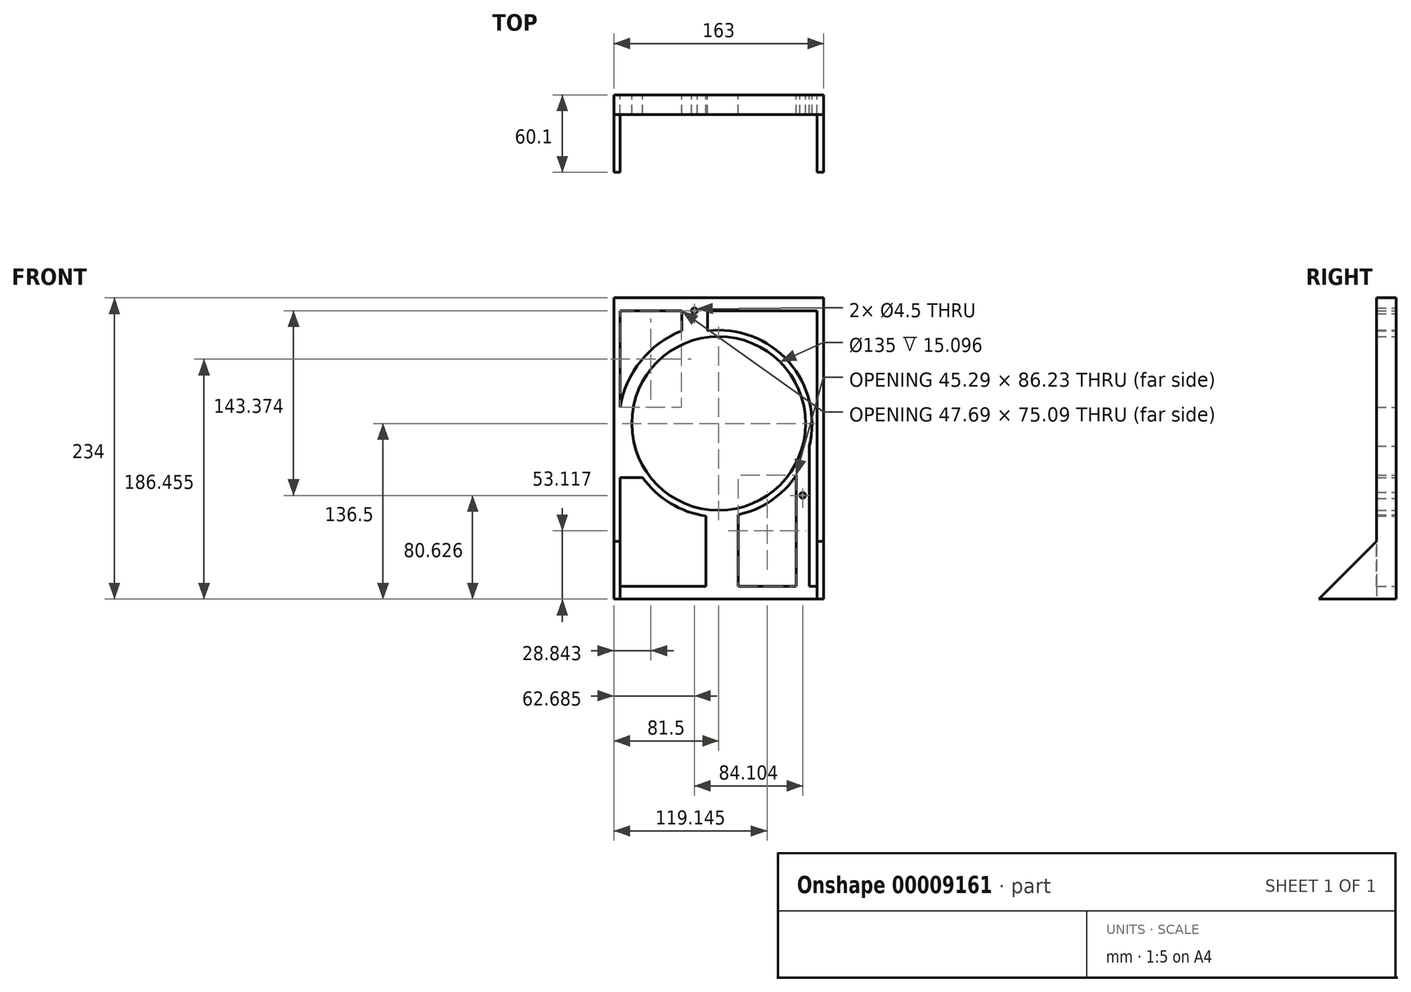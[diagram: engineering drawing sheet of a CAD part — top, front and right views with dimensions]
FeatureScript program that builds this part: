
annotation { "Feature Type Name" : "Feature", "Feature Type Description" : "" }
export const myFeature = defineFeature(function(context is Context, id is Id, definition is map)
    precondition{}
    {
        {
            var Q0;
            Q0=qCreatedBy(makeId("Front.planeOp"),FACE);
            var sketch = newSketch(context, id + "F0", { "sketchPlane" : qUnion([Q0])});
            skCircle(sketch, "E0", {"center": v(0, 0) * mm, "radius": 67.5 * mm});
            skLineSegment(sketch, "E1", {"start": v(-135.74, -136.5) * mm, "end": v(150.33, -136.5) * mm, "construction": true});
            skLineSegment(sketch, "E2", {"start": v(-81.5, 97.5) * mm, "end": v(-81.5, -136.5) * mm});
            skLineSegment(sketch, "E3.0.MirrorCS", {"start": v(81.5, 97.5) * mm, "end": v(81.5, -136.5) * mm});
            skCircle(sketch, "E4", {"center": v(65.29, -55.87) * mm, "radius": 2.25 * mm});
            skLineSegment(sketch, "E5", {"start": v(15, -70.93) * mm, "end": v(15, -126.5) * mm});
            skLineSegment(sketch, "E6", {"start": v(15, -126.5) * mm, "end": v(60.29, -126.5) * mm});
            skLineSegment(sketch, "E7", {"start": v(60.29, -126.5) * mm, "end": v(60.29, -40.27) * mm});
            skLineSegment(sketch, "E8.bottom", {"start": v(-10, -126.5) * mm, "end": v(-76.5, -126.5) * mm});
            skArc(sketch, "E9", {"start": v(15, -70.93) * mm, "mid": v(40.65, -60.03) * mm, "end": v(60.29, -40.27) * mm});
            skLineSegment(sketch, "E10", {"start": v(-81.5, -136.5) * mm, "end": v(81.5, -136.5) * mm});
            skLineSegment(sketch, "E11", {"start": v(-76.5, -42) * mm, "end": v(-59.1, -42) * mm});
            skLineSegment(sketch, "E12", {"start": v(-76.5, -42) * mm, "end": v(-76.5, -126.5) * mm});
            skArc(sketch, "E13", {"start": v(-59.1, -42) * mm, "mid": v(-37.63, -61.97) * mm, "end": v(-10, -71.8) * mm});
            skLineSegment(sketch, "E14", {"start": v(-10, -71.8) * mm, "end": v(-10, -126.5) * mm});
            skLineSegment(sketch, "E15.top", {"start": v(76.5, -126.5) * mm, "end": v(70.29, -126.5) * mm});
            skLineSegment(sketch, "E15.left", {"start": v(76.5, 87.5) * mm, "end": v(76.5, -126.5) * mm});
            skLineSegment(sketch, "E16", {"start": v(70.29, -126.5) * mm, "end": v(70.29, -17.77) * mm});
            skArc(sketch, "E17", {"start": v(70.29, -17.77) * mm, "mid": v(54.38, 47.94) * mm, "end": v(-8.81, 71.96) * mm});
            skLineSegment(sketch, "E18", {"start": v(-81.5, 97.5) * mm, "end": v(81.5, 97.5) * mm});
            skCircle(sketch, "E19", {"center": v(-18.81, 87.5) * mm, "radius": 2.25 * mm});
            skLineSegment(sketch, "E20", {"start": v(0, -136.5) * mm, "end": v(0, 97.5) * mm, "construction": true});
            skPoint(sketch, "E21", {"position": v(0, 67.5) * mm});
            skLineSegment(sketch, "E22", {"start": v(-76.5, 87.5) * mm, "end": v(-76.5, 12.4) * mm});
            skLineSegment(sketch, "E23", {"start": v(-76.5, 87.5) * mm, "end": v(-28.81, 87.5) * mm});
            skLineSegment(sketch, "E24", {"start": v(-28.81, 87.5) * mm, "end": v(-28.81, 71.94) * mm});
            skArc(sketch, "E25", {"start": v(-28.81, 71.94) * mm, "mid": v(-60.49, 48.45) * mm, "end": v(-76.5, 12.4) * mm});
            skLineSegment(sketch, "E26", {"start": v(-8.81, 71.96) * mm, "end": v(-8.81, 87.5) * mm});
            skLineSegment(sketch, "E27", {"start": v(-8.81, 87.5) * mm, "end": v(76.5, 87.5) * mm});
            skSolve(sketch);
        }
        {
            var Q0;
            Q0=makeQuery(id+"F0.imprint","IMPRINT",FACE,{"disambiguationData":[TD([[makeQuery(id+"F0.imprint","IMPRINT",EDGE,{"derivedFrom":sQuery(id+"F0.wireOp",EDGE,"E2")}),1.0]])]});
            extrude(context, id + "F1", {"entities" : qUnion([Q0]), "depth" : 15.1 * mm});
        }
        {
            var Q0;
            Q0=makeQuery(id+"F1.opExtrude","SWEPT_FACE",FACE,{"disambiguationData":[OSD([sQuery(id+"F0.wireOp",EDGE,"E2")])]});
            var sketch = newSketch(context, id + "F2", { "sketchPlane" : qUnion([Q0])});
            skLineSegment(sketch, "E28", {"start": v(15.1, -136.5) * mm, "end": v(60.1, -136.5) * mm});
            skLineSegment(sketch, "E29", {"start": v(60.1, -136.5) * mm, "end": v(15.1, -91.5) * mm});
            skLineSegment(sketch, "E30", {"start": v(15.1, -91.5) * mm, "end": v(15.1, -136.5) * mm});
            skSolve(sketch);
        }
        {
            var Q0;
            {var subQ6=sQuery(id+"F2.wireOp",EDGE,"E30");Q0=makeQuery(id+"F2.imprint","IMPRINT",FACE,{"disambiguationData":[TD([[makeQuery(id+"F2.imprint","IMPRINT",EDGE,{"derivedFrom":subQ6}),1.0]])]});}
            var Q1;
            {var subQ1=sQuery(id+"F2.wireOp",EDGE,"E29");var subQ3=sQuery(id+"F2.wireOp",EDGE,"E28");var subQ5=makeQuery(id+"F2.imprint","INTERSECT",VERTEX,{"derivedFrom":[subQ3,subQ1]});Q1=makeQuery(id+"F2.imprint","IMPRINT",FACE,{"disambiguationData":[TD([[makeQuery(id+"F2.imprint","IMPRINT",EDGE,{"disambiguationData":[TD([[subQ5,1.0]])],"derivedFrom":subQ3}),1.0]])]});}
            extrude(context, id + "F3", {"entities" : qUnion([Q0, Q1]), "operationType" : NewBodyOperationType.ADD, "oppositeDirection" : true, "depth" : 5 * mm});
        }
        {
            var Q0;
            Q0=makeQuery(id+"F1.opExtrude","SWEPT_FACE",FACE,{"disambiguationData":[OSD([sQuery(id+"F0.wireOp",EDGE,"E3.0.MirrorCS")])]});
            var sketch = newSketch(context, id + "F4", { "sketchPlane" : qUnion([Q0])});
            skLineSegment(sketch, "E31", {"start": v(-15.1, -91.5) * mm, "end": v(-60.1, -136.5) * mm});
            skLineSegment(sketch, "E32", {"start": v(-60.1, -136.5) * mm, "end": v(-15.1, -136.5) * mm});
            skLineSegment(sketch, "E33", {"start": v(-15.1, -136.5) * mm, "end": v(-15.1, -91.5) * mm});
            skSolve(sketch);
        }
        {
            var Q0;
            Q0=makeQuery(id+"F4.imprint","IMPRINT",FACE,{"disambiguationData":[TD([[makeQuery(id+"F4.imprint","IMPRINT",EDGE,{"derivedFrom":sQuery(id+"F4.wireOp",EDGE,"E31")}),1.0]])]});
            extrude(context, id + "F5", {"entities" : qUnion([Q0]), "operationType" : NewBodyOperationType.ADD, "oppositeDirection" : true, "depth" : 5 * mm});
        }
    });
